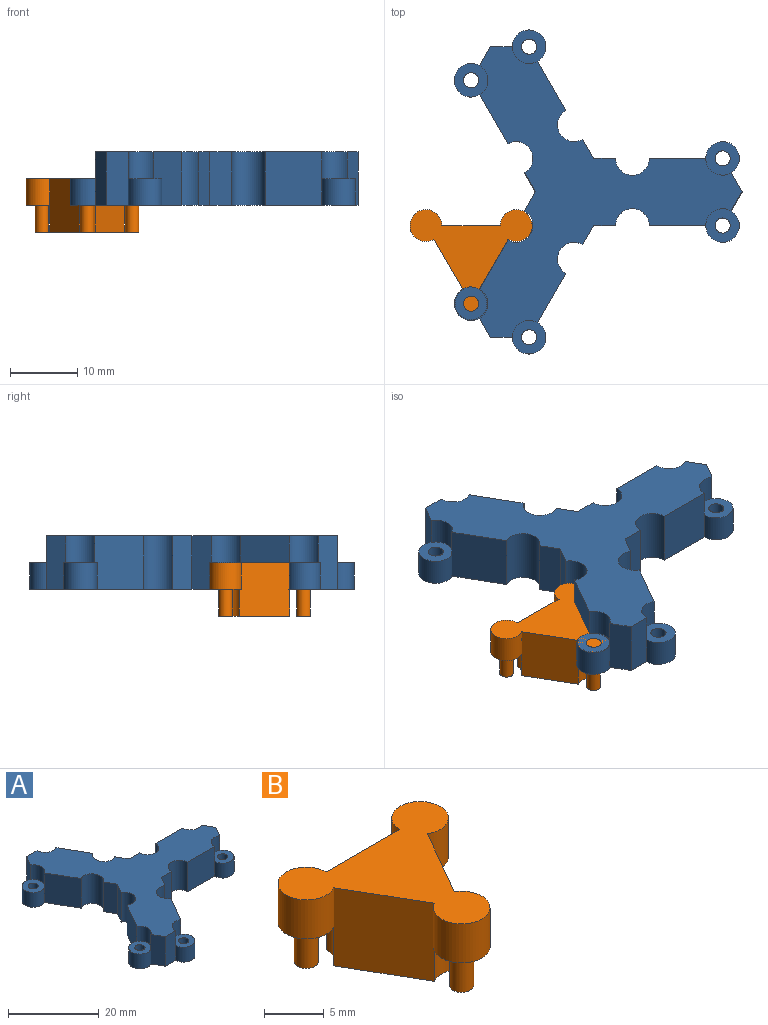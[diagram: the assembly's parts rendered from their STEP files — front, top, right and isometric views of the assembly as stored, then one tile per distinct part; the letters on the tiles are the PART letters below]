
ASSEMBLY  parts=2 mates=1
PART A: 50 faces, bbox 42.9x48.3x8 mm
  f0: cylinder r=2.5mm len=8mm, axis (0,0,-1), area 62.8mm2, adj f1,f29,f30,f43
  f1: plane 8x2.84mm, normal (0.87,-0.5,0), area 26.2mm2, adj f0,f2,f30,f43
  f2: plane 8x3.27mm, normal (0,-1,0), area 26.2mm2, adj f1,f3,f30,f43
  f3: cylinder r=2.5mm len=8mm, axis (0,0,-1), area 62.8mm2, adj f2,f4,f30,f43
  f4: plane 8.45x8mm, normal (0,-1,0), area 67.6mm2, adj f3,f5,f30,f37,f43
  f5: cylinder r=2.5mm len=4mm, axis (0,0,-1), area 20.9mm2, adj f4,f6,f30,f36
  f6: plane 8x2.84mm, normal (0.87,-0.5,0), area 26.2mm2, adj f5,f7,f30,f37,f43
  f7: plane 8x2.84mm, normal (0.87,0.5,0), area 26.2mm2, adj f6,f8,f30,f38,f43
  f8: cylinder r=2.5mm len=4mm, axis (0,0,-1), area 20.9mm2, adj f7,f9,f30,f35
  f9: plane 8.45x8mm, normal (0,1,0), area 67.6mm2, adj f8,f10,f30,f38,f43
  f10: cylinder r=2.5mm len=8mm, axis (0,0,-1), area 62.8mm2, adj f9,f11,f30,f43
  f11: plane 8x3.27mm, normal (0,1,0), area 26.2mm2, adj f10,f12,f30,f43
  f12: plane 8x2.84mm, normal (0.87,0.5,0), area 26.2mm2, adj f11,f13,f30,f43
  f13: cylinder r=2.5mm len=8mm, axis (0,0,-1), area 62.8mm2, adj f12,f14,f30,f43
  f14: plane 8x7.32mm, normal (0.87,0.5,0), area 67.6mm2, adj f13,f15,f30,f39,f43
  f15: cylinder r=2.5mm len=4mm, axis (0,0,-1), area 20.9mm2, adj f14,f16,f30,f34
  f16: plane 8x3.27mm, normal (0,1,0), area 26.2mm2, adj f15,f17,f30,f39,f43
  f17: plane 8x2.84mm, normal (-0.87,0.5,0), area 26.2mm2, adj f16,f18,f30,f40,f43
  f18: cylinder r=2.5mm len=4.33mm, axis (0,0,-1), area 20.9mm2, adj f17,f19,f30,f33
  f19: plane 8x7.32mm, normal (-0.87,-0.5,0), area 67.6mm2, adj f18,f20,f30,f40,f43
  f20: cylinder r=2.5mm len=8mm, axis (0,0,-1), area 62.8mm2, adj f19,f21,f30,f43
  f21: plane 8x2.84mm, normal (-0.87,-0.5,0), area 26.2mm2, adj f20,f22,f30,f43
  f22: plane 8x2.84mm, normal (-0.87,0.5,0), area 26.2mm2, adj f21,f23,f30,f43
  f23: cylinder r=2.5mm len=8mm, axis (0,0,-1), area 62.8mm2, adj f22,f24,f30,f43
  f24: plane 8x7.32mm, normal (-0.87,0.5,0), area 67.6mm2, adj f23,f25,f30,f41,f43
  f25: cylinder r=2.5mm len=4.33mm, axis (0,0,-1), area 20.9mm2, adj f24,f26,f30,f32
  f26: plane 8x2.84mm, normal (-0.87,-0.5,0), area 26.2mm2, adj f25,f27,f30,f41,f43
  f27: plane 8x3.27mm, normal (0,-1,0), area 26.2mm2, adj f26,f28,f30,f42,f43
  f28: cylinder r=2.5mm len=4mm, axis (0,0,-1), area 20.9mm2, adj f27,f29,f30,f31
  f29: plane 8x7.32mm, normal (0.87,-0.5,0), area 67.6mm2, adj f0,f28,f30,f42,f43
  f30: plane 43.3x39.14mm, normal (0,0,1), area 565.2mm2, adj f0,f1,f2,f3,f4,f5,f6,f7
  f31: plane 5x5mm, normal (0,0,1), area 15.7mm2, adj f28,f42,f46
  f32: plane 5x5mm, normal (0,0,1), area 15.7mm2, adj f25,f41,f47
  f33: plane 5x5mm, normal (0,0,1), area 15.7mm2, adj f18,f40,f48
  f34: plane 5x5mm, normal (0,0,1), area 15.7mm2, adj f15,f39,f49
  f35: plane 5x5mm, normal (0,0,1), area 15.7mm2, adj f8,f38,f44
  f36: plane 5x5mm, normal (0,0,1), area 15.7mm2, adj f5,f37,f45
  f37: cylinder r=2.5mm len=5mm, axis (0,0,1), area 41.9mm2, adj f4,f6,f36,f43
  f38: cylinder r=2.5mm len=5mm, axis (0,0,1), area 41.9mm2, adj f7,f9,f35,f43
  f39: cylinder r=2.5mm len=5mm, axis (0,0,1), area 41.9mm2, adj f14,f16,f34,f43
  f40: cylinder r=2.5mm len=5mm, axis (0,0,1), area 41.9mm2, adj f17,f19,f33,f43
  f41: cylinder r=2.5mm len=5mm, axis (0,0,1), area 41.9mm2, adj f24,f26,f32,f43
  f42: cylinder r=2.5mm len=5mm, axis (0,0,1), area 41.9mm2, adj f27,f29,f31,f43
  f43: plane 48.3x42.89mm, normal (0,0,-1), area 659.2mm2, adj f0,f1,f2,f3,f4,f6,f7,f9
  f44: cylinder r=1.12mm len=4mm, axis (0,0,1), area 28.3mm2, adj f35,f43
  f45: cylinder r=1.12mm len=4mm, axis (0,0,1), area 28.3mm2, adj f36,f43
  f46: cylinder r=1.12mm len=4mm, axis (0,0,1), area 28.3mm2, adj f31,f43
  f47: cylinder r=1.12mm len=4mm, axis (0,0,1), area 28.3mm2, adj f32,f43
  f48: cylinder r=1.12mm len=4mm, axis (0,0,1), area 28.3mm2, adj f33,f43
  f49: cylinder r=1.12mm len=4mm, axis (0,0,1), area 28.3mm2, adj f34,f43
PART B: 20 faces, bbox 18.2x16.4x8 mm
  f0: plane 4.75x4.75mm, normal (0,0,-1), area 14.6mm2, adj f4,f10,f15
  f1: plane 4.75x4.75mm, normal (0,0,-1), area 14.6mm2, adj f6,f11,f17
  f2: plane 4.75x4.75mm, normal (0,0,-1), area 14.6mm2, adj f8,f12,f19
  f3: plane 8.7x8mm, normal (0,1,0), area 69.6mm2, adj f4,f8,f9,f10,f12,f13
  f4: cylinder r=2.38mm len=4.75mm, axis (0,0,-1), area 49.7mm2, adj f0,f3,f5,f9
  f5: plane 8x7.54mm, normal (-0.87,-0.5,0), area 69.6mm2, adj f4,f6,f9,f10,f11,f13
  f6: cylinder r=2.38mm len=4.75mm, axis (0,0,-1), area 49.7mm2, adj f1,f5,f7,f9
  f7: plane 8x7.54mm, normal (0.87,-0.5,0), area 69.6mm2, adj f6,f8,f9,f11,f12,f13
  f8: cylinder r=2.38mm len=4.75mm, axis (0,0,-1), area 49.7mm2, adj f2,f3,f7,f9
  f9: plane 18.2x16.4mm, normal (0,0,1), area 122.7mm2, adj f3,f4,f5,f6,f7,f8
  f10: cylinder r=2.38mm len=4mm, axis (0,0,1), area 9.9mm2, adj f0,f3,f5,f13
  f11: cylinder r=2.38mm len=4mm, axis (0,0,1), area 9.9mm2, adj f1,f5,f7,f13
  f12: cylinder r=2.38mm len=4mm, axis (0,0,1), area 9.9mm2, adj f2,f3,f7,f13
  f13: plane 11.08x9.59mm, normal (0,0,-1), area 69.5mm2, adj f3,f5,f7,f10,f11,f12
  f14: plane 2x2mm, normal (0,0,-1), area 3.1mm2, adj f15
  f15: cylinder r=1mm len=4mm, axis (0,0,1), area 25.1mm2, adj f0,f14
  f16: plane 2x2mm, normal (0,0,-1), area 3.1mm2, adj f17
  f17: cylinder r=1mm len=4mm, axis (0,0,1), area 25.1mm2, adj f1,f16
  f18: plane 2x2mm, normal (0,0,-1), area 3.1mm2, adj f19
  f19: cylinder r=1mm len=4mm, axis (0,0,1), area 25.1mm2, adj f2,f18
PLACE A t=(-1.8,0,4)mm
PLACE B t=(-1.8,0,0)mm
MATE revolute A.f25 <-> B.f6  axis (0,0,-1) through (-17.19,-16.65,0)mm
